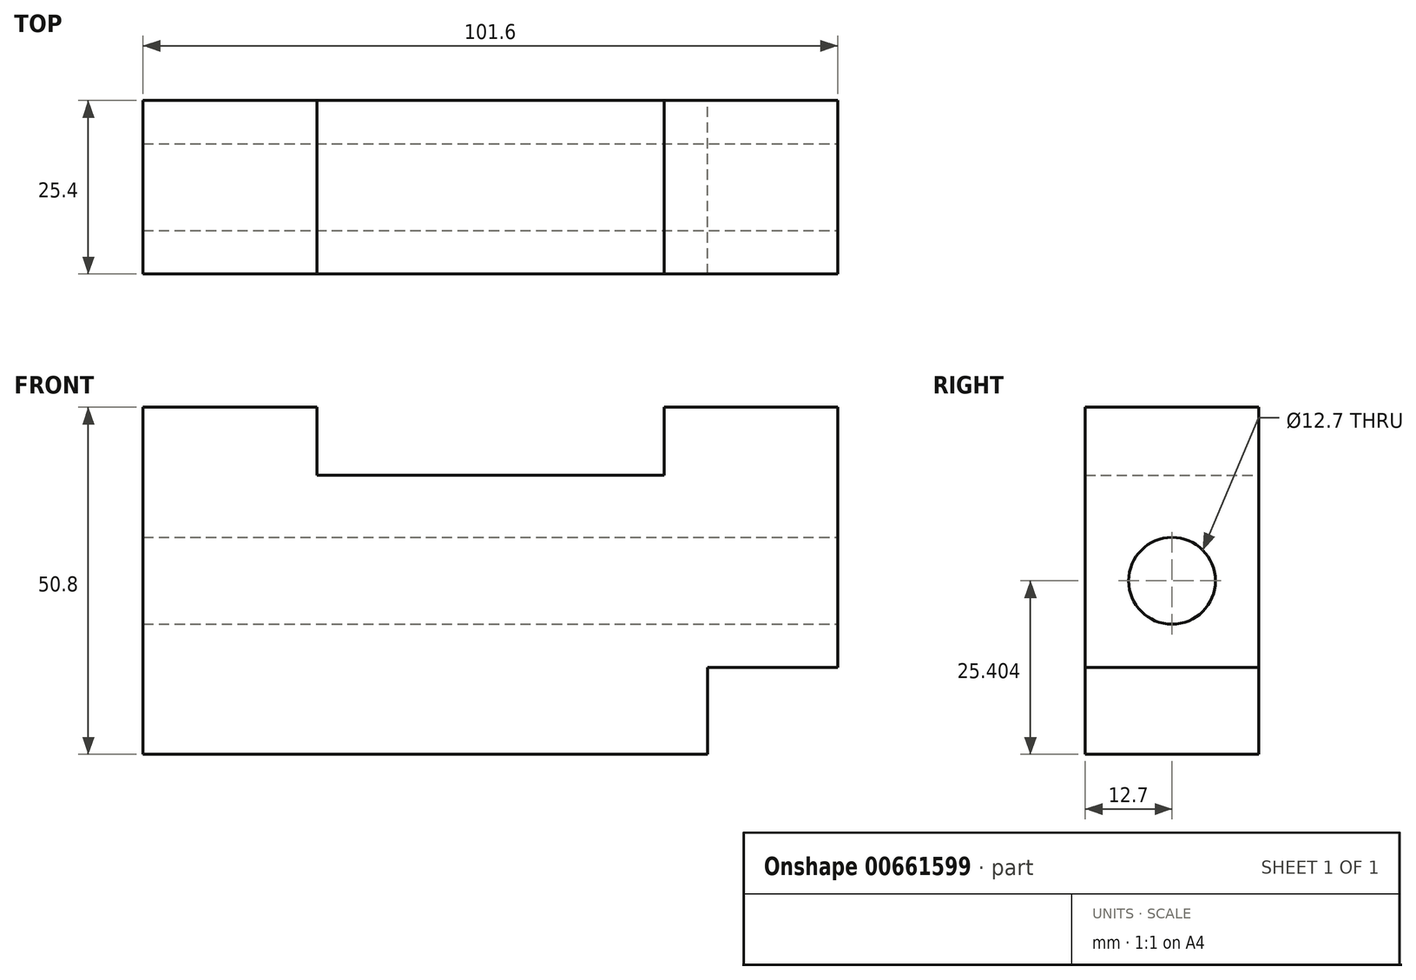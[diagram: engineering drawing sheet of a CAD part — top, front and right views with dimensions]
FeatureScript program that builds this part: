
annotation { "Feature Type Name" : "Feature", "Feature Type Description" : "" }
export const myFeature = defineFeature(function(context is Context, id is Id, definition is map)
    precondition{}
    {
        {
            var Q0;
            Q0=qCreatedBy(makeId("Front.planeOp"),FACE);
            var sketch = newSketch(context, id + "F0", { "sketchPlane" : qUnion([Q0])});
            skLineSegment(sketch, "E0", {"start": v(-101.6, 22.6) * mm, "end": v(-101.6, -28.2) * mm});
            skLineSegment(sketch, "E1", {"start": v(-101.6, -28.2) * mm, "end": v(-19.05, -28.2) * mm});
            skLineSegment(sketch, "E2", {"start": v(-19.05, -28.2) * mm, "end": v(-19.05, -15.5) * mm});
            skLineSegment(sketch, "E3", {"start": v(-19.05, -15.5) * mm, "end": v(0, -15.5) * mm});
            skLineSegment(sketch, "E4", {"start": v(0, -15.5) * mm, "end": v(0, 22.6) * mm});
            skLineSegment(sketch, "E5", {"start": v(0, 22.6) * mm, "end": v(-25.4, 22.6) * mm});
            skLineSegment(sketch, "E6", {"start": v(-25.4, 22.6) * mm, "end": v(-25.4, 12.65) * mm});
            skLineSegment(sketch, "E7", {"start": v(-25.4, 12.65) * mm, "end": v(-76.2, 12.65) * mm});
            skLineSegment(sketch, "E8", {"start": v(-76.2, 12.65) * mm, "end": v(-76.2, 22.6) * mm});
            skLineSegment(sketch, "E9", {"start": v(-76.2, 22.6) * mm, "end": v(-101.6, 22.6) * mm});
            skSolve(sketch);
        }
        {
            var Q0;
            Q0=makeQuery(id+"F0.imprint","IMPRINT",FACE,{"disambiguationData":[TD([[makeQuery(id+"F0.imprint","IMPRINT",EDGE,{"derivedFrom":sQuery(id+"F0.wireOp",EDGE,"E0")}),1.0]])]});
            extrude(context, id + "F1", {"entities" : qUnion([Q0]), "depth" : 25.4 * mm, "offsetDistance" : 25.4 * mm});
        }
        {
            var Q0;
            Q0=qCreatedBy(makeId("Right.planeOp"),FACE);
            var sketch = newSketch(context, id + "F2", { "sketchPlane" : qUnion([Q0])});
            skCircle(sketch, "E10", {"center": v(-12.7, -2.8) * mm, "radius": 6.35 * mm});
            skPoint(sketch, "E10.centerSnap0", {"position": v(-25.4, 3.54) * mm});
            skSolve(sketch);
        }
        {
            var Q0;
            Q0=makeQuery(id+"F2.imprint","IMPRINT",FACE,{"disambiguationData":[TD([[makeQuery(id+"F2.imprint","IMPRINT",EDGE,{"derivedFrom":sQuery(id+"F2.wireOp",EDGE,"E10")}),1.0]])]});
            extrude(context, id + "F3", {"entities" : qUnion([Q0]), "operationType" : NewBodyOperationType.REMOVE, "endBound" : BoundingType.THROUGH_ALL, "oppositeDirection" : true, "depth" : 25.4 * mm, "offsetDistance" : 25.4 * mm});
        }
    });
